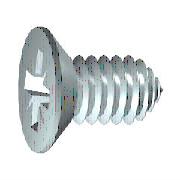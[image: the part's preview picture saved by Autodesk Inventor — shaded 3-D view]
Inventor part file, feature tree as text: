
AUTODESK INVENTOR PART (.ipt)
format: ipt  version: 2020 (Build 240168000, 168)  size: 267,776 bytes
history: native  units: mm (DEFAULTED — no unit token found)
features: extrude x2, plane x1, sketch x1
ambient origin geometry x8: Origin, YZ Plane, XZ Plane, XY Plane, X Axis, Y Axis, Z Axis, Center Point
bodies: Solid1 (feature_tree), Body (feature_tree)
feature tree (4):
  extrude  "Slot"  TaperAngle=45.0deg  [1 undecoded]
  extrude  "Star Cut"  Depth=2.05mm
  plane  "Work Plane2"
  sketch  "Sketch3"  dims[d0=22.0mm d2=45.0deg d3=3.5mm d5=7.3mm d6=4.1mm d7=4.625123mm d8=10.821041mm d9=2.2mm d16=90.0deg d10=45.0deg d11=1.64mm d12=4.1mm d13=0.515mm d14=4.1mm d15=45.0deg d17=0.515mm d18=2.35mm d19=-5.235988mm d20=19.65mm d21=0.0mm d22=1.75mm d23=3.2mm d25=0.0mm d26=2.05mm d66=25.4mm d27=0.872665mm d28=0.206mm d29=2.35mm d71=45.0deg d73=0.0mm d74=0.0mm]
note: 1 required parameter value undecoded (feature->parameter linkage not recoverable at this tier; creation-order binding heuristic only, values carry confidence <= 0.55)
